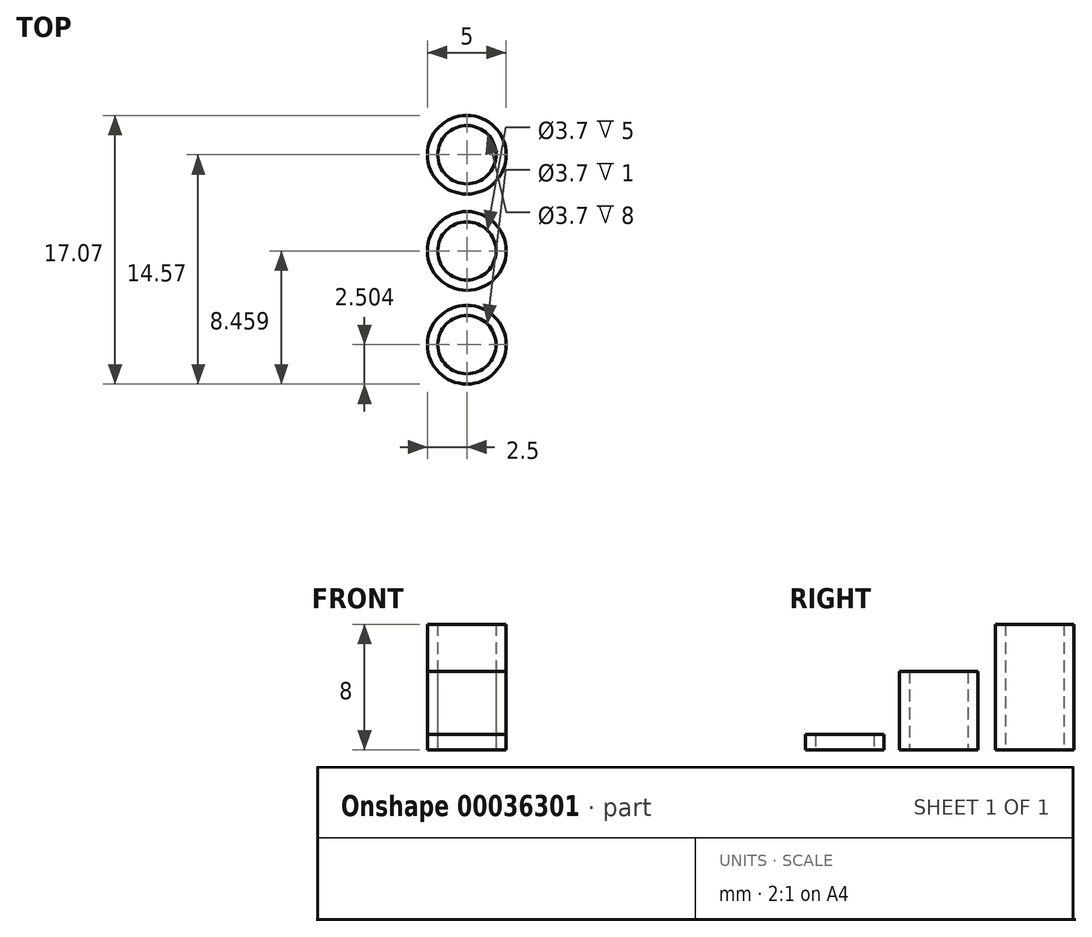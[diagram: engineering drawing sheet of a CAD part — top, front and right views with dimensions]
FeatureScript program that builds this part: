
annotation { "Feature Type Name" : "Feature", "Feature Type Description" : "" }
export const myFeature = defineFeature(function(context is Context, id is Id, definition is map)
    precondition{}
    {
        {
            var Q0;
            Q0=qCreatedBy(makeId("Top.planeOp"),FACE);
            var sketch = newSketch(context, id + "F0", { "sketchPlane" : qUnion([Q0])});
            skCircle(sketch, "E0", {"center": v(0, 0) * mm, "radius": 2.5 * mm});
            skCircle(sketch, "E1", {"center": v(0, 0) * mm, "radius": 1.85 * mm});
            skCircle(sketch, "E2", {"center": v(0, -6.11) * mm, "radius": 2.5 * mm});
            skCircle(sketch, "E3", {"center": v(0, -6.11) * mm, "radius": 1.85 * mm});
            skCircle(sketch, "E4", {"center": v(0, -12.07) * mm, "radius": 2.5 * mm});
            skCircle(sketch, "E5", {"center": v(0, -12.07) * mm, "radius": 1.85 * mm});
            skSolve(sketch);
        }
        {
            var Q0;
            Q0=makeQuery(id+"F0.imprint","IMPRINT",FACE,{"disambiguationData":[TD([[makeQuery(id+"F0.imprint","IMPRINT",EDGE,{"derivedFrom":sQuery(id+"F0.wireOp",EDGE,"E0")}),1.0]])]});
            extrude(context, id + "F1", {"entities" : qUnion([Q0]), "depth" : 8 * mm});
        }
        {
            var Q0;
            Q0=makeQuery(id+"F0.imprint","IMPRINT",FACE,{"disambiguationData":[TD([[makeQuery(id+"F0.imprint","IMPRINT",EDGE,{"derivedFrom":sQuery(id+"F0.wireOp",EDGE,"E2")}),1.0]])]});
            extrude(context, id + "F2", {"entities" : qUnion([Q0]), "depth" : 5 * mm});
        }
        {
            var Q0;
            Q0=makeQuery(id+"F0.imprint","IMPRINT",FACE,{"disambiguationData":[TD([[makeQuery(id+"F0.imprint","IMPRINT",EDGE,{"derivedFrom":sQuery(id+"F0.wireOp",EDGE,"E4")}),1.0]])]});
            extrude(context, id + "F3", {"entities" : qUnion([Q0]), "depth" : 1 * mm});
        }
    });
